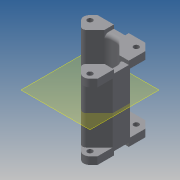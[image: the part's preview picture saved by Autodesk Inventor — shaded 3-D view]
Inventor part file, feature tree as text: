
AUTODESK INVENTOR PART (.ipt)
format: ipt  version: 2013 (Build 170138000, 138)  size: 301,568 bytes
history: native  units: mm
features: extrude x6, sketch x6, fillet x4, projected_geometry x4, chamfer x1, plane x1, mirror x1
ambient origin geometry x8: Origin, YZ Plane, XZ Plane, XY Plane, X Axis, Y Axis, Z Axis, Center Point
bodies: Solid1 (feature_tree)
feature tree (23):
  extrude  "Extrusion1"  Depth=42.0mm
  extrude  "Extrusion2"  Depth=3.5mm
  extrude  "Extrusion3"  Depth=5.0mm
  extrude  "Extrusion4"  Depth=5.0mm
  chamfer  "Chamfer1"  Distance=5.0mm
  fillet  "Fillet3"  Radius=5.0mm
  extrude  "Extrusion5"  Depth=3.0mm
  plane  "Work Plane1"
  mirror  "Mirror1"
  fillet  "Fillet4"  Radius=40.0mm
  extrude  "Extrusion6"  Depth=40.0mm TaperAngle=0.0deg
  fillet  "Fillet5"  Radius=5.0mm
  fillet  "Fillet6"  Radius=5.0mm
  sketch  "Sketch1"  dims[d0=31.0mm d1=42.0mm]
  sketch  "Sketch2"  dims[d2=22.5mm d3=3.5mm]
  sketch  "Sketch3"  dims[d4=5.0mm d5=0.0mm d6=5.0mm]
  sketch  "Sketch4"  dims[d8=3.0mm d9=5.0mm]
  projected_geometry  "Projected Loop1"
  projected_geometry  "Projected Loop2"
  projected_geometry  "Projected Loop3"
  sketch  "Sketch5"  dims[d10=3.0mm]
  sketch  "Sketch6"  dims[d11=45.0deg d12=5.0mm d13=5.0mm d14=3.0mm d15=40.0mm d16=0.0mm d17=40.0mm d18=0.0mm d19=5.0mm d20=0.0mm d23=5.0mm d24=2.0mm d25=45.0deg d26=5.5mm d27=10.0mm d29=2.5mm d30=0.0mm d31=2.5mm d32=4.243mm d33=2.5mm d34=0.0mm d35=4.24mm d36=2.5mm]
  projected_geometry  "Projected Loop4"
